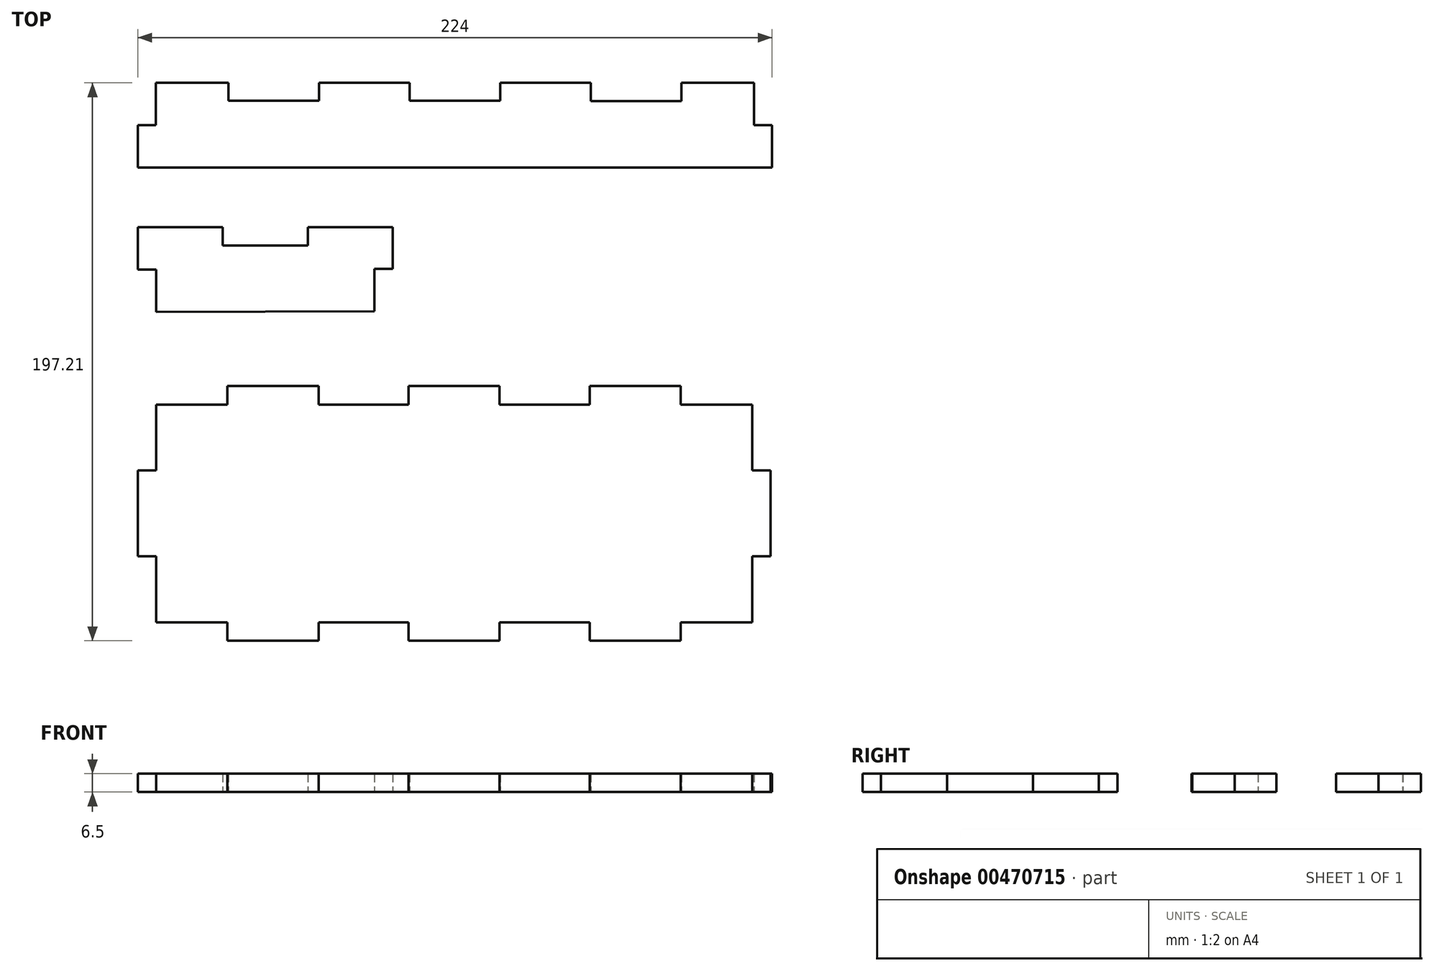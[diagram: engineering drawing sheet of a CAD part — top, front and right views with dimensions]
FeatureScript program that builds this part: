
annotation { "Feature Type Name" : "Feature", "Feature Type Description" : "" }
export const myFeature = defineFeature(function(context is Context, id is Id, definition is map)
    precondition{}
    {
        {
            var Q0;
            Q0=qCreatedBy(makeId("Top.planeOp"),FACE);
            var sketch = newSketch(context, id + "F0", { "sketchPlane" : qUnion([Q0])});
            skLineSegment(sketch, "E0", {"start": v(32, 30) * mm, "end": v(32, 23.7) * mm});
            skLineSegment(sketch, "E1", {"start": v(32, 23.7) * mm, "end": v(64, 23.7) * mm});
            skLineSegment(sketch, "E2", {"start": v(64, 23.7) * mm, "end": v(64, 30) * mm});
            skLineSegment(sketch, "E3", {"start": v(64, 30) * mm, "end": v(96, 30) * mm});
            skLineSegment(sketch, "E4", {"start": v(96, 30) * mm, "end": v(96, 23.7) * mm});
            skLineSegment(sketch, "E5", {"start": v(96, 23.7) * mm, "end": v(128, 23.7) * mm});
            skLineSegment(sketch, "E6", {"start": v(128, 23.7) * mm, "end": v(128, 30) * mm});
            skLineSegment(sketch, "E7", {"start": v(128, 30) * mm, "end": v(160, 30) * mm});
            skLineSegment(sketch, "E8", {"start": v(0, 0) * mm, "end": v(0, 15) * mm});
            skLineSegment(sketch, "E9", {"start": v(0, 15) * mm, "end": v(6.3, 15) * mm});
            skLineSegment(sketch, "E10", {"start": v(6.3, 30) * mm, "end": v(6.3, 15) * mm});
            skLineSegment(sketch, "E11", {"start": v(6.3, 30) * mm, "end": v(32, 30) * mm});
            skLineSegment(sketch, "E12", {"start": v(160, 30) * mm, "end": v(160, 23.5) * mm});
            skLineSegment(sketch, "E13", {"start": v(160, 23.5) * mm, "end": v(192, 23.5) * mm});
            skLineSegment(sketch, "E14", {"start": v(192, 23.5) * mm, "end": v(192, 30) * mm});
            skLineSegment(sketch, "E15", {"start": v(192, 30) * mm, "end": v(217.7, 30) * mm});
            skLineSegment(sketch, "E16", {"start": v(217.7, 30) * mm, "end": v(217.7, 15) * mm});
            skLineSegment(sketch, "E17", {"start": v(217.7, 15) * mm, "end": v(224, 15) * mm});
            skLineSegment(sketch, "E18", {"start": v(224, 15) * mm, "end": v(224, 0) * mm});
            skLineSegment(sketch, "E19", {"start": v(0, 0) * mm, "end": v(224, 0) * mm});
            skSolve(sketch);
        }
        {
            var Q0;
            Q0=makeQuery(id+"F0.imprint","IMPRINT",FACE,{"disambiguationData":[TD([[makeQuery(id+"F0.imprint","IMPRINT",EDGE,{"derivedFrom":sQuery(id+"F0.wireOp",EDGE,"E0")}),-1.0]])]});
            extrude(context, id + "F1", {"entities" : qUnion([Q0]), "depth" : 6.5 * mm});
        }
        {
            var Q0;
            Q0=qCreatedBy(makeId("Top.planeOp"),FACE);
            var sketch = newSketch(context, id + "F2", { "sketchPlane" : qUnion([Q0])});
            skLineSegment(sketch, "E20", {"start": v(0, -21) * mm, "end": v(0, -36) * mm});
            skLineSegment(sketch, "E21", {"start": v(0, -36) * mm, "end": v(6.5, -36) * mm});
            skLineSegment(sketch, "E22", {"start": v(6.5, -36) * mm, "end": v(6.5, -51) * mm});
            skLineSegment(sketch, "E23", {"start": v(0, -21) * mm, "end": v(30, -21) * mm});
            skLineSegment(sketch, "E24", {"start": v(30, -21) * mm, "end": v(30, -27.5) * mm});
            skLineSegment(sketch, "E25", {"start": v(30, -27.5) * mm, "end": v(60, -27.5) * mm});
            skLineSegment(sketch, "E26", {"start": v(60, -27.5) * mm, "end": v(60, -21) * mm});
            skLineSegment(sketch, "E27", {"start": v(60, -21) * mm, "end": v(90, -21) * mm});
            skLineSegment(sketch, "E28", {"start": v(90, -21) * mm, "end": v(90, -35.75) * mm});
            skLineSegment(sketch, "E29", {"start": v(90, -35.75) * mm, "end": v(83.5, -35.75) * mm});
            skLineSegment(sketch, "E30", {"start": v(83.5, -35.75) * mm, "end": v(83.5, -50.75) * mm});
            skLineSegment(sketch, "E31", {"start": v(83.5, -50.75) * mm, "end": v(6.5, -51) * mm});
            skSolve(sketch);
        }
        {
            var Q0;
            Q0=makeQuery(id+"F2.imprint","IMPRINT",FACE,{"disambiguationData":[TD([[makeQuery(id+"F2.imprint","IMPRINT",EDGE,{"derivedFrom":sQuery(id+"F2.wireOp",EDGE,"E20")}),1.0]])]});
            extrude(context, id + "F3", {"entities" : qUnion([Q0]), "depth" : 6.5 * mm});
        }
        {
            var Q0;
            Q0=qCreatedBy(makeId("Top.planeOp"),FACE);
            var sketch = newSketch(context, id + "F4", { "sketchPlane" : qUnion([Q0])});
            skLineSegment(sketch, "E32", {"start": v(6.5, -107.01) * mm, "end": v(0, -107.01) * mm});
            skLineSegment(sketch, "E33", {"start": v(0, -107.01) * mm, "end": v(0, -137.41) * mm});
            skLineSegment(sketch, "E34", {"start": v(0, -137.41) * mm, "end": v(6.5, -137.41) * mm});
            skLineSegment(sketch, "E35", {"start": v(6.5, -137.41) * mm, "end": v(6.5, -160.71) * mm});
            skLineSegment(sketch, "E36", {"start": v(6.5, -160.71) * mm, "end": v(31.6, -160.71) * mm});
            skLineSegment(sketch, "E37", {"start": v(31.6, -167.21) * mm, "end": v(31.6, -160.71) * mm});
            skLineSegment(sketch, "E38", {"start": v(31.6, -167.21) * mm, "end": v(63.8, -167.21) * mm});
            skLineSegment(sketch, "E39", {"start": v(63.8, -160.71) * mm, "end": v(63.8, -167.21) * mm});
            skLineSegment(sketch, "E40", {"start": v(63.8, -160.71) * mm, "end": v(95.6, -160.71) * mm});
            skLineSegment(sketch, "E41", {"start": v(95.6, -167.21) * mm, "end": v(95.6, -160.71) * mm});
            skLineSegment(sketch, "E42", {"start": v(95.6, -167.21) * mm, "end": v(127.8, -167.21) * mm});
            skLineSegment(sketch, "E43", {"start": v(127.8, -160.71) * mm, "end": v(127.8, -167.21) * mm});
            skLineSegment(sketch, "E44", {"start": v(127.8, -160.71) * mm, "end": v(159.6, -160.71) * mm});
            skLineSegment(sketch, "E45", {"start": v(159.6, -83.71) * mm, "end": v(127.8, -83.71) * mm});
            skLineSegment(sketch, "E46", {"start": v(127.8, -77.21) * mm, "end": v(127.8, -83.71) * mm});
            skLineSegment(sketch, "E47", {"start": v(127.8, -77.21) * mm, "end": v(95.6, -77.21) * mm});
            skLineSegment(sketch, "E48", {"start": v(95.6, -83.71) * mm, "end": v(95.6, -77.21) * mm});
            skLineSegment(sketch, "E49", {"start": v(95.6, -83.71) * mm, "end": v(63.8, -83.71) * mm});
            skLineSegment(sketch, "E50", {"start": v(63.8, -77.21) * mm, "end": v(63.8, -83.71) * mm});
            skLineSegment(sketch, "E51", {"start": v(63.8, -77.21) * mm, "end": v(31.6, -77.21) * mm});
            skLineSegment(sketch, "E52", {"start": v(31.6, -83.71) * mm, "end": v(31.6, -77.21) * mm});
            skLineSegment(sketch, "E53", {"start": v(6.5, -83.71) * mm, "end": v(31.6, -83.71) * mm});
            skLineSegment(sketch, "E54", {"start": v(6.5, -107.01) * mm, "end": v(6.5, -83.71) * mm});
            skLineSegment(sketch, "E55", {"start": v(159.6, -83.71) * mm, "end": v(159.6, -77.21) * mm});
            skLineSegment(sketch, "E56", {"start": v(159.6, -77.21) * mm, "end": v(191.8, -77.21) * mm});
            skLineSegment(sketch, "E57", {"start": v(191.8, -77.21) * mm, "end": v(191.8, -83.71) * mm});
            skLineSegment(sketch, "E58", {"start": v(191.8, -83.71) * mm, "end": v(217, -83.71) * mm});
            skLineSegment(sketch, "E59", {"start": v(217, -83.71) * mm, "end": v(217, -107.01) * mm});
            skLineSegment(sketch, "E60", {"start": v(217, -107.01) * mm, "end": v(223.5, -107.01) * mm});
            skLineSegment(sketch, "E61", {"start": v(223.5, -107.01) * mm, "end": v(223.5, -137.41) * mm});
            skLineSegment(sketch, "E62", {"start": v(223.5, -137.41) * mm, "end": v(217, -137.41) * mm});
            skLineSegment(sketch, "E63", {"start": v(217, -137.41) * mm, "end": v(217, -160.71) * mm});
            skLineSegment(sketch, "E64", {"start": v(217, -160.71) * mm, "end": v(191.8, -160.71) * mm});
            skLineSegment(sketch, "E65", {"start": v(191.8, -160.71) * mm, "end": v(191.8, -167.21) * mm});
            skLineSegment(sketch, "E66", {"start": v(191.8, -167.21) * mm, "end": v(159.6, -167.21) * mm});
            skLineSegment(sketch, "E67", {"start": v(159.6, -167.21) * mm, "end": v(159.6, -160.71) * mm});
            skSolve(sketch);
        }
        {
            var Q0;
            Q0=makeQuery(id+"F4.imprint","IMPRINT",FACE,{"disambiguationData":[TD([[makeQuery(id+"F4.imprint","IMPRINT",EDGE,{"derivedFrom":sQuery(id+"F4.wireOp",EDGE,"E32")}),1.0]])]});
            extrude(context, id + "F5", {"entities" : qUnion([Q0]), "depth" : 6.5 * mm});
        }
    });
